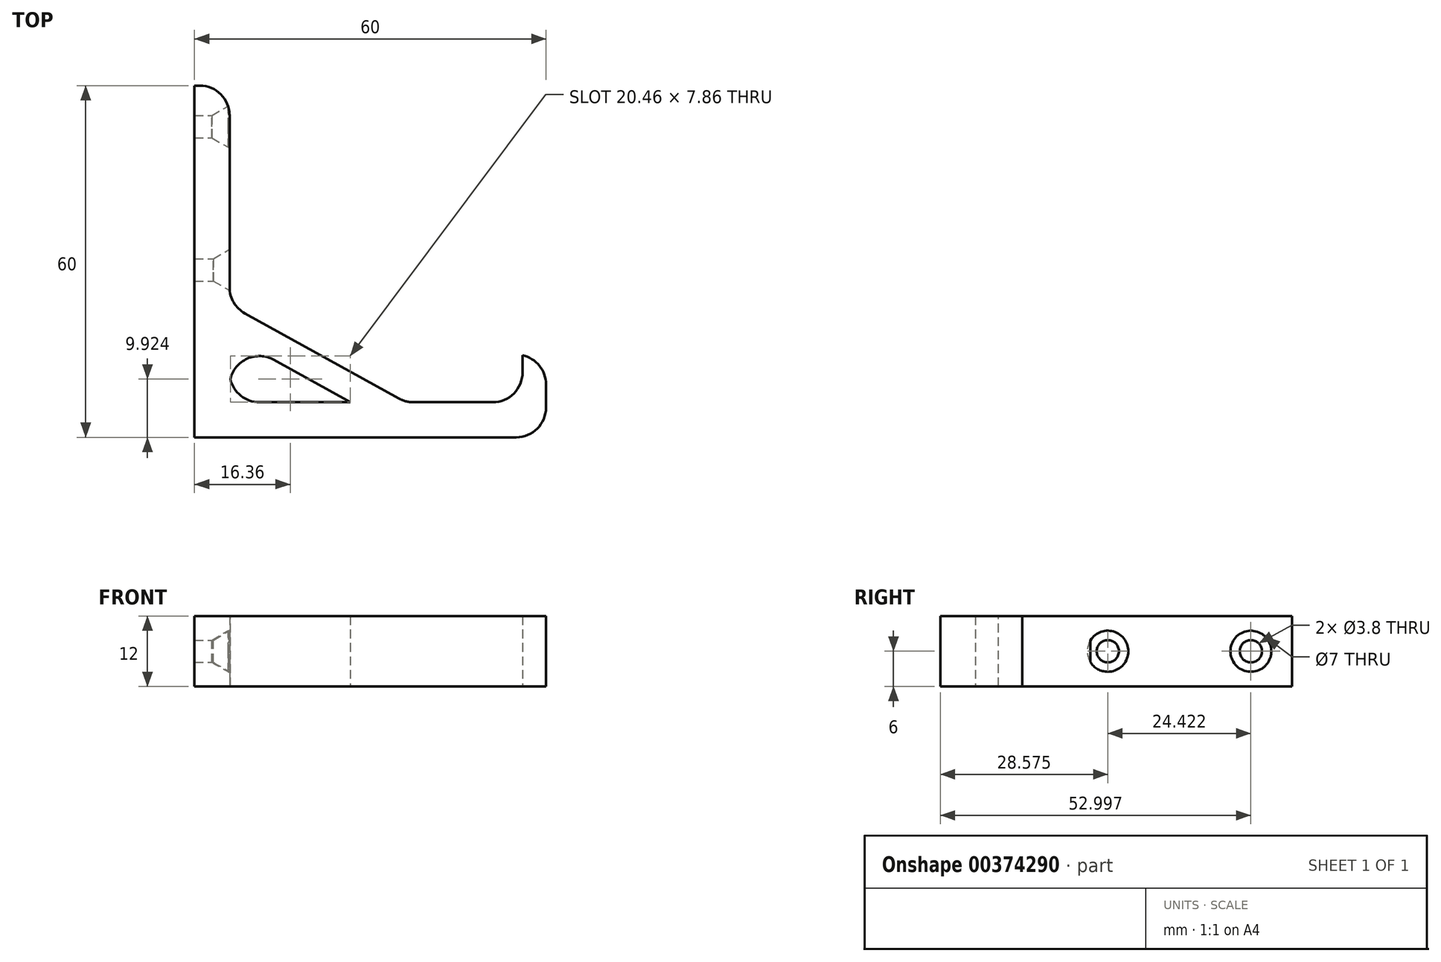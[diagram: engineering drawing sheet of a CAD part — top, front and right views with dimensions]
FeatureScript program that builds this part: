
annotation { "Feature Type Name" : "Feature", "Feature Type Description" : "" }
export const myFeature = defineFeature(function(context is Context, id is Id, definition is map)
    precondition{}
    {
        {
            var Q0;
            Q0=qCreatedBy(makeId("Top.planeOp"),FACE);
            var sketch = newSketch(context, id + "F0", { "sketchPlane" : qUnion([Q0])});
            skLineSegment(sketch, "E0", {"start": v(-40.06, 27.79) * mm, "end": v(-40.06, -32.21) * mm});
            skLineSegment(sketch, "E1", {"start": v(-40.06, -32.21) * mm, "end": v(19.94, -32.21) * mm});
            skLineSegment(sketch, "E2", {"start": v(19.94, -32.21) * mm, "end": v(19.94, -26.21) * mm});
            skLineSegment(sketch, "E3", {"start": v(-40.06, 27.79) * mm, "end": v(-34.06, 27.79) * mm});
            skLineSegment(sketch, "E4", {"start": v(-34.06, 27.79) * mm, "end": v(-34.06, -26.21) * mm});
            skLineSegment(sketch, "E5", {"start": v(-34.06, -26.21) * mm, "end": v(19.94, -26.21) * mm});
            skLineSegment(sketch, "E6", {"start": v(19.94, -26.21) * mm, "end": v(19.94, -18.21) * mm});
            skLineSegment(sketch, "E7", {"start": v(19.94, -18.21) * mm, "end": v(15.94, -18.21) * mm});
            skLineSegment(sketch, "E8", {"start": v(15.94, -18.21) * mm, "end": v(15.94, -26.21) * mm});
            skLineSegment(sketch, "E9", {"start": v(0, -26.21) * mm, "end": v(15.94, -26.21) * mm});
            skLineSegment(sketch, "E10", {"start": v(15.94, -26.21) * mm, "end": v(-4.06, -26.21) * mm});
            skLineSegment(sketch, "E11", {"start": v(-4.06, -26.21) * mm, "end": v(-34.06, -9.6) * mm});
            skLineSegment(sketch, "E12", {"start": v(-34.06, -14.81) * mm, "end": v(-13.47, -26.21) * mm});
            skSolve(sketch);
        }
        {
            var Q0;
            Q0=makeQuery(id+"F0.imprint","IMPRINT",FACE,{"disambiguationData":[TD([[makeQuery(id+"F0.imprint","IMPRINT",EDGE,{"derivedFrom":sQuery(id+"F0.wireOp",EDGE,"E0")}),1.0]])]});
            var Q1;
            {var subQ0=sQuery(id+"F0.wireOp",EDGE,"E11");Q1=makeQuery(id+"F0.imprint","IMPRINT",FACE,{"disambiguationData":[TD([[makeQuery(id+"F0.imprint","IMPRINT",EDGE,{"derivedFrom":subQ0}),1.0]])]});}
            var Q2;
            {var subQ0=sQuery(id+"F0.wireOp",EDGE,"E6");Q2=makeQuery(id+"F0.imprint","IMPRINT",FACE,{"disambiguationData":[TD([[makeQuery(id+"F0.imprint","IMPRINT",EDGE,{"derivedFrom":subQ0}),1.0]])]});}
            extrude(context, id + "F1", {"entities" : qUnion([Q0, Q1, Q2]), "depth" : 12 * mm});
        }
        {
            var Q0;
            {var subQ0=sQuery(id+"F0.wireOp",EDGE,"E4");Q0=makeQuery(id+"F1.opExtrude","SWEPT_FACE",FACE,{"disambiguationData":[OSD([subQ0]),TDD([makeQuery(id+"F0.imprint","IMPRINT",EDGE,{"disambiguationData":[TD([[makeQuery(id+"F0.imprint","INTERSECT",VERTEX,{"derivedFrom":[sQuery(id+"F0.wireOp",EDGE,"E3"),subQ0]}),-1.0]])],"derivedFrom":subQ0})])]});}
            var sketch = newSketch(context, id + "F2", { "sketchPlane" : qUnion([Q0])});
            skLineSegment(sketch, "E13", {"start": v(27.79, 6) * mm, "end": v(20.79, 6) * mm});
            skLineSegment(sketch, "E14", {"start": v(20.79, 6) * mm, "end": v(-3.63, 6) * mm});
            skSolve(sketch);
        }
        {
            var Q0;
            Q0=makeQuery(id+"F1.opExtrude","SWEPT_EDGE",EDGE,{"disambiguationData":[OSD([sQuery(id+"F0.wireOp",EDGE,"E3"),sQuery(id+"F0.wireOp",EDGE,"E4")])]});
            var Q1;
            Q1=makeQuery(id+"F1.opExtrude","SWEPT_EDGE",EDGE,{"disambiguationData":[OSD([sQuery(id+"F0.wireOp",EDGE,"E4"),sQuery(id+"F0.wireOp",EDGE,"E11")])]});
            var Q2;
            Q2=makeQuery(id+"F1.opExtrude","SWEPT_EDGE",EDGE,{"disambiguationData":[OSD([sQuery(id+"F0.wireOp",EDGE,"E5"),sQuery(id+"F0.wireOp",EDGE,"E10"),sQuery(id+"F0.wireOp",EDGE,"E11")])]});
            var Q3;
            Q3=makeQuery(id+"F1.opExtrude","SWEPT_EDGE",EDGE,{"disambiguationData":[OSD([sQuery(id+"F0.wireOp",EDGE,"E5"),sQuery(id+"F0.wireOp",EDGE,"E8"),sQuery(id+"F0.wireOp",EDGE,"E10")])]});
            var Q4;
            Q4=makeQuery(id+"F1.opExtrude","SWEPT_EDGE",EDGE,{"disambiguationData":[OSD([sQuery(id+"F0.wireOp",EDGE,"E6"),sQuery(id+"F0.wireOp",EDGE,"E7")])]});
            var Q5;
            Q5=makeQuery(id+"F1.opExtrude","SWEPT_EDGE",EDGE,{"disambiguationData":[OSD([sQuery(id+"F0.wireOp",EDGE,"E1"),sQuery(id+"F0.wireOp",EDGE,"E2")])]});
            var Q6;
            Q6=makeQuery(id+"F1.opExtrude","SWEPT_EDGE",EDGE,{"disambiguationData":[OSD([sQuery(id+"F0.wireOp",EDGE,"E4"),sQuery(id+"F0.wireOp",EDGE,"E5")])]});
            var Q7;
            Q7=makeQuery(id+"F1.opExtrude","SWEPT_EDGE",EDGE,{"disambiguationData":[OSD([sQuery(id+"F0.wireOp",EDGE,"E4"),sQuery(id+"F0.wireOp",EDGE,"E12")])]});
            fillet(context, id + "F3", {"entities" : qUnion([Q0, Q1, Q2, Q3, Q4, Q5, Q6, Q7]), "radius" : 5.08 * mm, "tangentPropagation" : true, "allowEdgeOverflow" : false});
        }
        {
            var Q0;
            Q0=sQuery(id+"F2.wireOp",VERTEX,"E14.start");
            var Q1;
            Q1=sQuery(id+"F2.wireOp",VERTEX,"E14.end");
            var Q2;
            Q2=makeQuery(id+"F1.opExtrude","SWEPT_BODY",BODY,{"disambiguationData":[OSD([sQuery(id+"F0.wireOp",EDGE,"E0"),sQuery(id+"F0.wireOp",EDGE,"E1"),sQuery(id+"F0.wireOp",EDGE,"E2"),sQuery(id+"F0.wireOp",EDGE,"E3"),sQuery(id+"F0.wireOp",EDGE,"E4"),sQuery(id+"F0.wireOp",EDGE,"E5"),sQuery(id+"F0.wireOp",EDGE,"E6"),sQuery(id+"F0.wireOp",EDGE,"E7"),sQuery(id+"F0.wireOp",EDGE,"E8"),sQuery(id+"F0.wireOp",EDGE,"E10"),sQuery(id+"F0.wireOp",EDGE,"E11"),sQuery(id+"F0.wireOp",EDGE,"E12")])]});
            hole(context, id + "F4", {"style" : HoleStyle.C_SINK, "endStyle" : HoleEndStyle.BLIND, "holeDiameter" : 3.8 * mm, "cSinkDiameter" : 7 * mm, "cSinkAngle" : 60 * degree, "holeDepth" : 20 * mm, "isTappedThrough" : true, "tappedDepth" : 12.7 * mm, "tapClearance" : 3, "locations" : qUnion([Q0, Q1]), "scope" : qUnion([Q2])});
        }
    });
